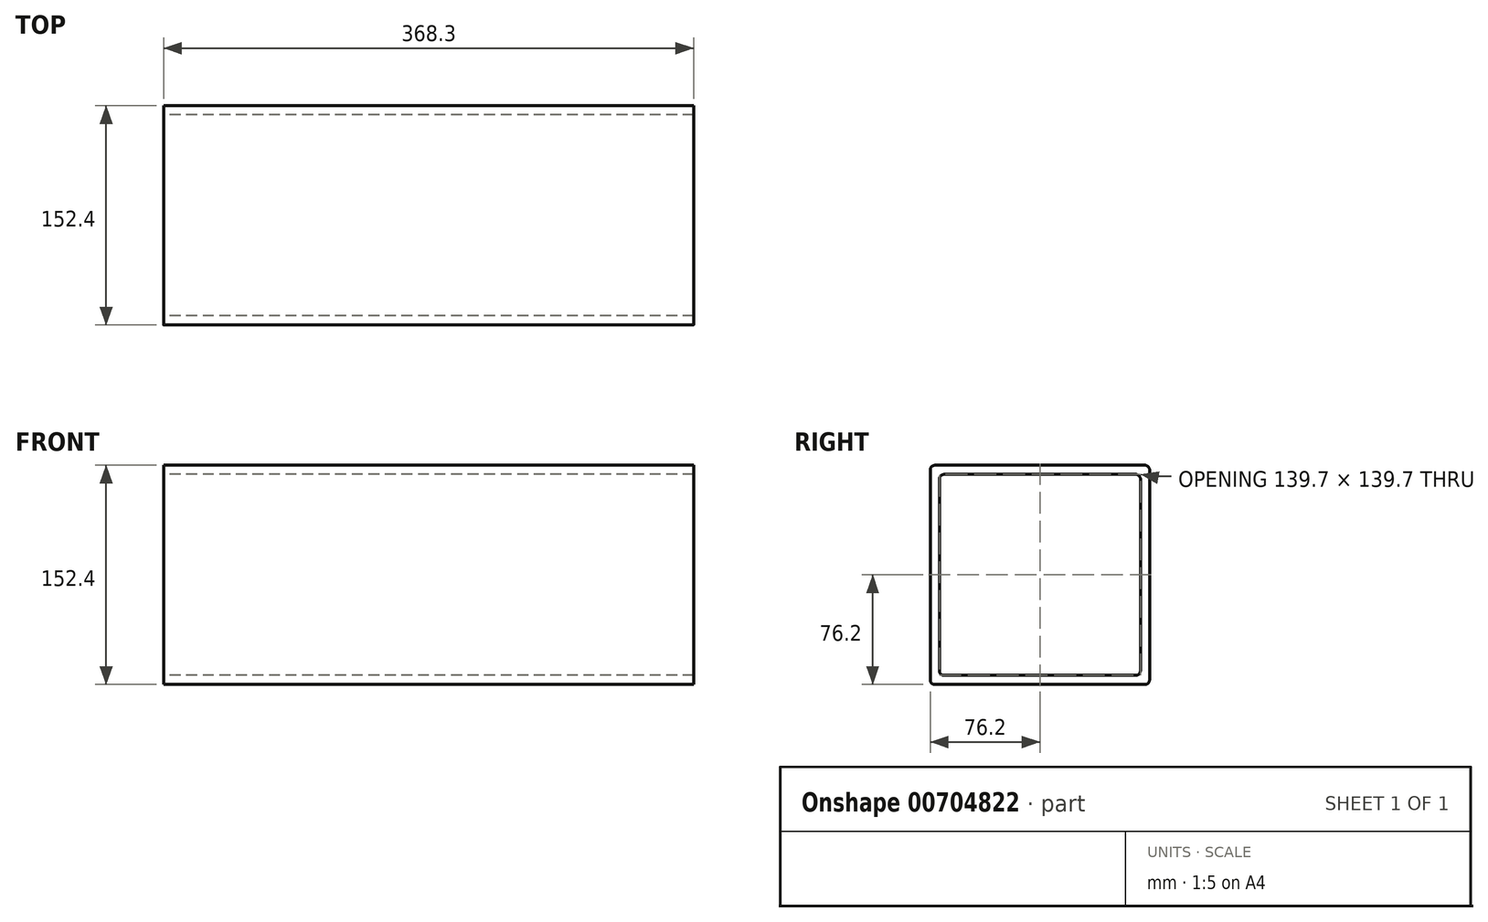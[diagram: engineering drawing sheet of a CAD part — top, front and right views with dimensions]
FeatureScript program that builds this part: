
annotation { "Feature Type Name" : "Feature", "Feature Type Description" : "" }
export const myFeature = defineFeature(function(context is Context, id is Id, definition is map)
    precondition{}
    {
        {
            var Q0;
            Q0=qCreatedBy(makeId("Right.planeOp"),FACE);
            var sketch = newSketch(context, id + "F0", { "sketchPlane" : qUnion([Q0])});
            skLineSegment(sketch, "E0.bottom", {"start": v(-73.03, 76.2) * mm, "end": v(73.03, 76.2) * mm});
            skLineSegment(sketch, "E0.top", {"start": v(-73.03, -76.2) * mm, "end": v(73.02, -76.2) * mm});
            skLineSegment(sketch, "E0.left", {"start": v(-76.2, 73.02) * mm, "end": v(-76.2, -73.03) * mm});
            skLineSegment(sketch, "E0.right", {"start": v(76.2, 73.02) * mm, "end": v(76.2, -73.03) * mm});
            skPoint(sketch, "E0.middle", {"position": v(0, 0) * mm});
            skLineSegment(sketch, "E1.0", {"start": v(-69.85, 66.68) * mm, "end": v(-69.85, -66.67) * mm});
            skLineSegment(sketch, "E2.3", {"start": v(-66.68, -69.85) * mm, "end": v(66.68, -69.85) * mm});
            skLineSegment(sketch, "E3.0", {"start": v(69.85, 66.68) * mm, "end": v(69.85, -66.67) * mm});
            skLineSegment(sketch, "E3.1", {"start": v(-66.68, 69.85) * mm, "end": v(66.68, 69.85) * mm});
            skPoint(sketch, "E4.visualSharp", {"position": v(-76.2, 76.2) * mm});
            skArc(sketch, "E4.filletArc", {"start": v(-73.03, 76.2) * mm, "mid": v(-75.27, 75.27) * mm, "end": v(-76.2, 73.02) * mm});
            skPoint(sketch, "E5.visualSharp", {"position": v(76.2, 76.2) * mm});
            skArc(sketch, "E5.filletArc", {"start": v(76.2, 73.02) * mm, "mid": v(75.27, 75.27) * mm, "end": v(73.03, 76.2) * mm});
            skPoint(sketch, "E6.visualSharp", {"position": v(76.2, -76.2) * mm});
            skArc(sketch, "E6.filletArc", {"start": v(73.02, -76.2) * mm, "mid": v(75.27, -75.27) * mm, "end": v(76.2, -73.03) * mm});
            skPoint(sketch, "E7.visualSharp", {"position": v(-76.2, -76.2) * mm});
            skArc(sketch, "E7.filletArc", {"start": v(-76.2, -73.03) * mm, "mid": v(-75.27, -75.27) * mm, "end": v(-73.03, -76.2) * mm});
            skPoint(sketch, "E8.visualSharp", {"position": v(-69.85, -69.85) * mm});
            skArc(sketch, "E8.filletArc", {"start": v(-69.85, -66.67) * mm, "mid": v(-68.92, -68.92) * mm, "end": v(-66.68, -69.85) * mm});
            skPoint(sketch, "E9.visualSharp", {"position": v(-69.85, 69.85) * mm});
            skArc(sketch, "E9.filletArc", {"start": v(-66.68, 69.85) * mm, "mid": v(-68.92, 68.92) * mm, "end": v(-69.85, 66.68) * mm});
            skPoint(sketch, "E10.visualSharp", {"position": v(69.85, 69.85) * mm});
            skArc(sketch, "E10.filletArc", {"start": v(69.85, 66.68) * mm, "mid": v(68.92, 68.92) * mm, "end": v(66.68, 69.85) * mm});
            skPoint(sketch, "E11.visualSharp", {"position": v(69.85, -69.85) * mm});
            skArc(sketch, "E11.filletArc", {"start": v(66.68, -69.85) * mm, "mid": v(68.92, -68.92) * mm, "end": v(69.85, -66.67) * mm});
            skSolve(sketch);
        }
        {
            var Q0;
            Q0=makeQuery(id+"F0.imprint","IMPRINT",FACE,{"disambiguationData":[TD([[makeQuery(id+"F0.imprint","IMPRINT",EDGE,{"derivedFrom":sQuery(id+"F0.wireOp",EDGE,"E0.bottom")}),-1.0]])]});
            extrude(context, id + "F1", {"entities" : qUnion([Q0]), "flatOperationType" : FlatOperationType.REMOVE, "depth" : 368.3 * mm, "offsetDistance" : 25.4 * mm, "domain" : OperationDomain.MODEL});
        }
    });
